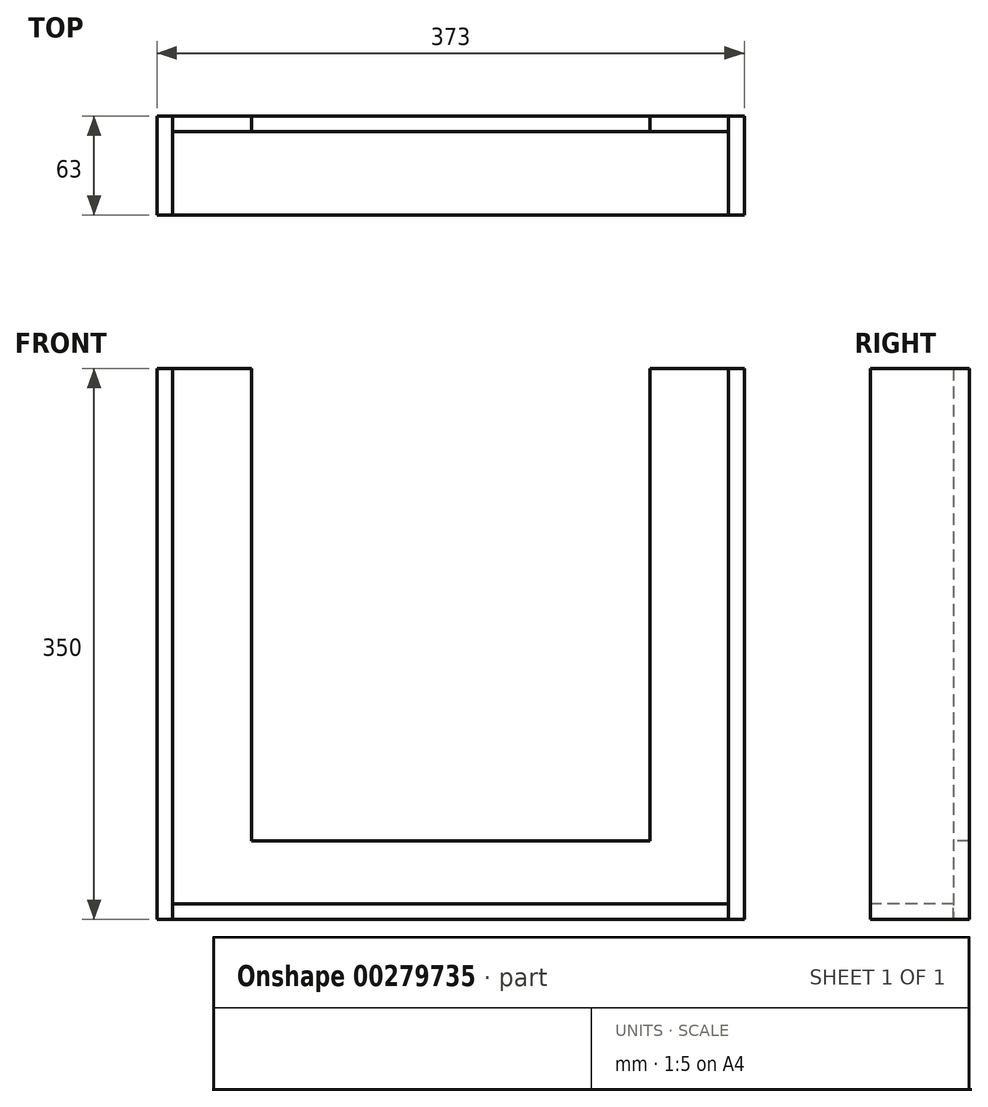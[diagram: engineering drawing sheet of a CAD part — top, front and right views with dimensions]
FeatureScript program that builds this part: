
annotation { "Feature Type Name" : "Feature", "Feature Type Description" : "" }
export const myFeature = defineFeature(function(context is Context, id is Id, definition is map)
    precondition{}
    {
        {
            var Q0;
            Q0=qCreatedBy(makeId("Front.planeOp"),FACE);
            var sketch = newSketch(context, id + "F0", { "sketchPlane" : qUnion([Q0])});
            skLineSegment(sketch, "E0.bottom", {"start": v(0, 0) * mm, "end": v(353, 0) * mm});
            skLineSegment(sketch, "E0.top", {"start": v(0, 10) * mm, "end": v(353, 10) * mm});
            skLineSegment(sketch, "E0.left", {"start": v(0, 0) * mm, "end": v(0, 10) * mm});
            skLineSegment(sketch, "E0.right", {"start": v(353, 0) * mm, "end": v(353, 10) * mm});
            skLineSegment(sketch, "E1.bottom", {"start": v(353, 0) * mm, "end": v(363, 0) * mm});
            skLineSegment(sketch, "E1.top", {"start": v(353, 350) * mm, "end": v(363, 350) * mm});
            skLineSegment(sketch, "E1.left", {"start": v(353, 0) * mm, "end": v(353, 350) * mm});
            skLineSegment(sketch, "E1.right", {"start": v(363, 0) * mm, "end": v(363, 350) * mm});
            skLineSegment(sketch, "E2.bottom", {"start": v(0, 0) * mm, "end": v(-10, 0) * mm});
            skLineSegment(sketch, "E2.top", {"start": v(0, 350) * mm, "end": v(-10, 350) * mm});
            skLineSegment(sketch, "E2.left", {"start": v(0, 0) * mm, "end": v(0, 350) * mm});
            skLineSegment(sketch, "E2.right", {"start": v(-10, 0) * mm, "end": v(-10, 350) * mm});
            skSolve(sketch);
        }
        {
            var Q0;
            {var subQ3=sQuery(id+"F0.wireOp",EDGE,"E2.bottom");Q0=makeQuery(id+"F0.imprint","IMPRINT",FACE,{"disambiguationData":[TD([[makeQuery(id+"F0.imprint","IMPRINT",EDGE,{"derivedFrom":subQ3}),-1.0]])]});}
            var Q1;
            {var subQ3=sQuery(id+"F0.wireOp",EDGE,"E1.bottom");Q1=makeQuery(id+"F0.imprint","IMPRINT",FACE,{"disambiguationData":[TD([[makeQuery(id+"F0.imprint","IMPRINT",EDGE,{"derivedFrom":subQ3}),1.0]])]});}
            extrude(context, id + "F1", {"entities" : qUnion([Q0, Q1]), "oppositeDirection" : true, "depth" : 63 * mm});
        }
        {
            var Q0;
            Q0=qCreatedBy(makeId("Front.planeOp"),FACE);
            var sketch = newSketch(context, id + "F2", { "sketchPlane" : qUnion([Q0])});
            skLineSegment(sketch, "E3.bottom", {"start": v(0, 0) * mm, "end": v(353, 0) * mm});
            skLineSegment(sketch, "E3.top", {"start": v(0, 10) * mm, "end": v(353, 10) * mm});
            skLineSegment(sketch, "E3.left", {"start": v(0, 0) * mm, "end": v(0, 10) * mm});
            skLineSegment(sketch, "E3.right", {"start": v(353, 0) * mm, "end": v(353, 10) * mm});
            skSolve(sketch);
        }
        {
            var Q0;
            Q0 = qSketchRegion(id + "F2", true);
            extrude(context, id + "F3", {"entities" : qUnion([Q0]), "oppositeDirection" : true, "depth" : 53 * mm});
        }
        {
            var Q0;
            Q0=makeQuery(id+"F3.opExtrude","CAP_FACE",FACE,{"disambiguationData":[OSD([sQuery(id+"F2.wireOp",EDGE,"E3.bottom"),sQuery(id+"F2.wireOp",EDGE,"E3.top"),sQuery(id+"F2.wireOp",EDGE,"E3.left"),sQuery(id+"F2.wireOp",EDGE,"E3.right")])],"isStart":false});
            var sketch = newSketch(context, id + "F4", { "sketchPlane" : qUnion([Q0])});
            skLineSegment(sketch, "E4", {"start": v(0, 0) * mm, "end": v(0, 350) * mm});
            skLineSegment(sketch, "E5", {"start": v(0, 350) * mm, "end": v(-50, 350) * mm});
            skLineSegment(sketch, "E6", {"start": v(-50, 350) * mm, "end": v(-50, 50) * mm});
            skLineSegment(sketch, "E7", {"start": v(-50, 50) * mm, "end": v(-303, 50) * mm});
            skLineSegment(sketch, "E8", {"start": v(-303, 50) * mm, "end": v(-303, 350) * mm});
            skLineSegment(sketch, "E9", {"start": v(-303, 350) * mm, "end": v(-353, 350) * mm});
            skLineSegment(sketch, "E10", {"start": v(-353, 350) * mm, "end": v(-353, 0) * mm});
            skLineSegment(sketch, "E11", {"start": v(-353, 0) * mm, "end": v(0, 0) * mm});
            skSolve(sketch);
        }
        {
            var Q0;
            Q0 = qSketchRegion(id + "F4", true);
            extrude(context, id + "F5", {"entities" : qUnion([Q0]), "depth" : 10 * mm});
        }
    });
